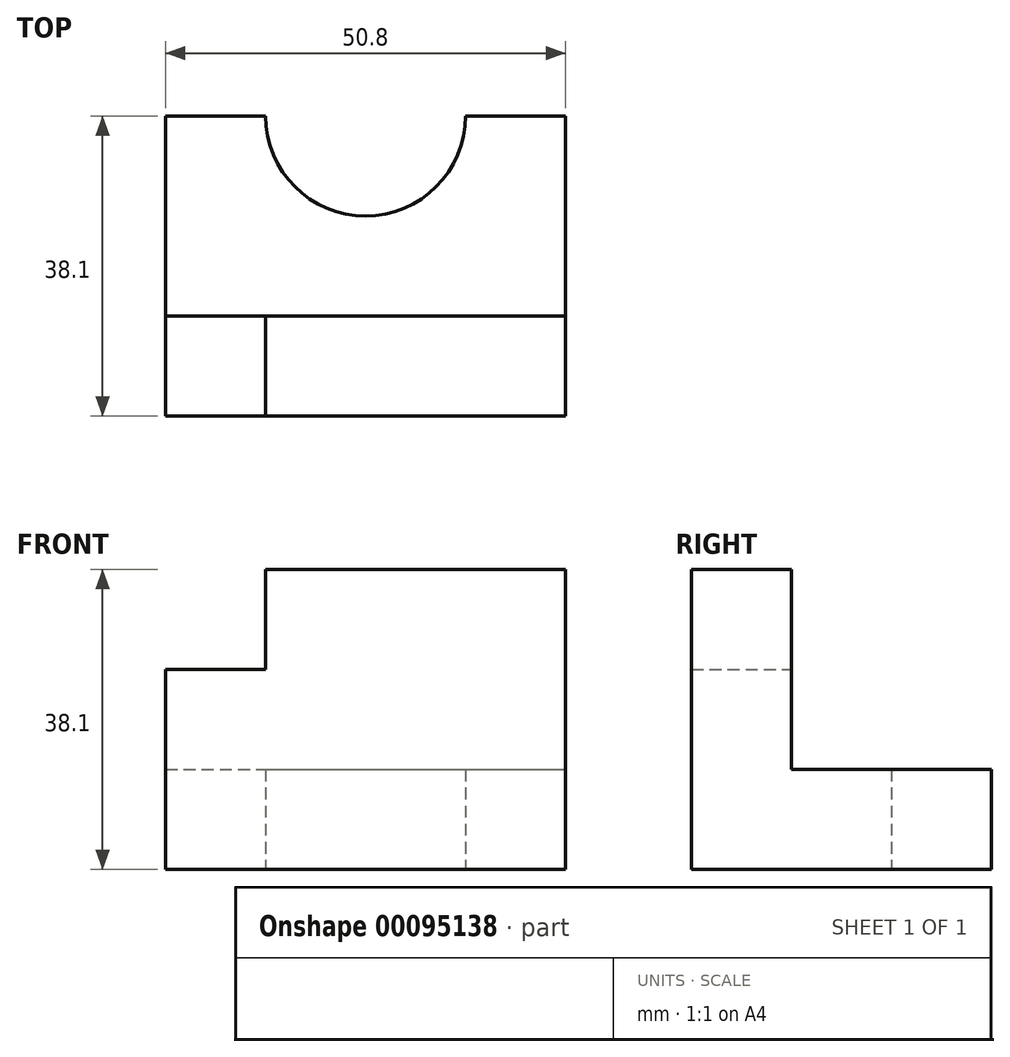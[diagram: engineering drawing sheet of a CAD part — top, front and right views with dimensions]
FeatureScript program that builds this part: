
annotation { "Feature Type Name" : "Feature", "Feature Type Description" : "" }
export const myFeature = defineFeature(function(context is Context, id is Id, definition is map)
    precondition{}
    {
        {
            var Q0;
            Q0=qCreatedBy(makeId("Top.planeOp"),FACE);
            var sketch = newSketch(context, id + "F0", { "sketchPlane" : qUnion([Q0])});
            skLineSegment(sketch, "E0.bottom", {"start": v(-25.4, 0) * mm, "end": v(25.4, 0) * mm});
            skLineSegment(sketch, "E0.top", {"start": v(-25.4, 38.1) * mm, "end": v(25.4, 38.1) * mm});
            skLineSegment(sketch, "E0.left", {"start": v(-25.4, 0) * mm, "end": v(-25.4, 38.1) * mm});
            skLineSegment(sketch, "E0.right", {"start": v(25.4, 0) * mm, "end": v(25.4, 38.1) * mm});
            skArc(sketch, "E1", {"start": v(-25.4, 38.1) * mm, "mid": v(0, 63.5) * mm, "end": v(25.4, 38.1) * mm});
            skCircle(sketch, "E2", {"center": v(0, 38.1) * mm, "radius": 12.7 * mm});
            skSolve(sketch);
        }
        {
            var Q0;
            Q0=makeQuery(id+"F0.imprint","IMPRINT",FACE,{"disambiguationData":[TD([[makeQuery(id+"F0.imprint","IMPRINT",EDGE,{"derivedFrom":sQuery(id+"F0.wireOp",EDGE,"E0.bottom")}),1.0]])]});
            var Q1;
            {var subQ0=sQuery(id+"F0.wireOp",EDGE,"E1");Q1=makeQuery(id+"F0.imprint","IMPRINT",FACE,{"disambiguationData":[TD([[makeQuery(id+"F0.imprint","IMPRINT",EDGE,{"derivedFrom":subQ0}),-1.0]])]});}
            extrude(context, id + "F1", {"entities" : qUnion([Q0, Q1]), "depth" : 12.7 * mm});
        }
        {
            var Q0;
            Q0=makeQuery(id+"F1.opExtrude","CAP_FACE",FACE,{"disambiguationData":[OSD([sQuery(id+"F0.wireOp",EDGE,"E0.bottom"),sQuery(id+"F0.wireOp",EDGE,"E0.left"),sQuery(id+"F0.wireOp",EDGE,"E0.right"),sQuery(id+"F0.wireOp",EDGE,"E1"),sQuery(id+"F0.wireOp",EDGE,"E2")])],"isStart":false});
            var sketch = newSketch(context, id + "F2", { "sketchPlane" : qUnion([Q0])});
            skLineSegment(sketch, "E3.bottom", {"start": v(-25.4, 0) * mm, "end": v(25.4, 0) * mm});
            skLineSegment(sketch, "E3.top", {"start": v(-25.4, 12.7) * mm, "end": v(25.4, 12.7) * mm});
            skLineSegment(sketch, "E3.left", {"start": v(-25.4, 0) * mm, "end": v(-25.4, 12.7) * mm});
            skLineSegment(sketch, "E3.right", {"start": v(25.4, 0) * mm, "end": v(25.4, 12.7) * mm});
            skLineSegment(sketch, "E4.bottom", {"start": v(-25.4, 12.7) * mm, "end": v(-12.7, 12.7) * mm});
            skLineSegment(sketch, "E4.top", {"start": v(-25.4, 0) * mm, "end": v(-12.7, 0) * mm});
            skLineSegment(sketch, "E4.left", {"start": v(-25.4, 12.7) * mm, "end": v(-25.4, 0) * mm});
            skLineSegment(sketch, "E4.right", {"start": v(-12.7, 12.7) * mm, "end": v(-12.7, 0) * mm});
            skSolve(sketch);
        }
        {
            var Q0;
            Q0=makeQuery(id+"F2.imprint","IMPRINT",FACE,{"disambiguationData":[TD([[makeQuery(id+"F2.imprint","IMPRINT",EDGE,{"derivedFrom":sQuery(id+"F2.wireOp",EDGE,"E3.bottom")}),1.0]])]});
            var Q1;
            Q1=makeQuery(id+"F2.imprint","IMPRINT",FACE,{"disambiguationData":[TD([[makeQuery(id+"F2.imprint","IMPRINT",EDGE,{"derivedFrom":sQuery(id+"F2.wireOp",EDGE,"E4.bottom")}),-1.0]])]});
            extrude(context, id + "F3", {"entities" : qUnion([Q0, Q1]), "operationType" : NewBodyOperationType.ADD, "depth" : 25.4 * mm});
        }
        {
            var Q0;
            Q0=makeQuery(id+"F3.opExtrude","CAP_FACE",FACE,{"disambiguationData":[OSD([sQuery(id+"F2.wireOp",EDGE,"E3.bottom"),sQuery(id+"F2.wireOp",EDGE,"E3.top"),sQuery(id+"F2.wireOp",EDGE,"E3.right"),sQuery(id+"F2.wireOp",EDGE,"E4.bottom"),sQuery(id+"F2.wireOp",EDGE,"E4.top"),sQuery(id+"F2.wireOp",EDGE,"E4.left")])],"isStart":false});
            var sketch = newSketch(context, id + "F4", { "sketchPlane" : qUnion([Q0])});
            skLineSegment(sketch, "E5.bottom", {"start": v(-25.4, 12.7) * mm, "end": v(-12.7, 12.7) * mm});
            skLineSegment(sketch, "E5.top", {"start": v(-25.4, 0) * mm, "end": v(-12.7, 0) * mm});
            skLineSegment(sketch, "E5.left", {"start": v(-25.4, 12.7) * mm, "end": v(-25.4, 0) * mm});
            skLineSegment(sketch, "E5.right", {"start": v(-12.7, 12.7) * mm, "end": v(-12.7, 0) * mm});
            skSolve(sketch);
        }
        {
            var Q0;
            Q0=makeQuery(id+"F4.imprint","IMPRINT",FACE,{"disambiguationData":[TD([[makeQuery(id+"F4.imprint","IMPRINT",EDGE,{"derivedFrom":sQuery(id+"F4.wireOp",EDGE,"E5.bottom")}),-1.0]])]});
            extrude(context, id + "F5", {"entities" : qUnion([Q0]), "operationType" : NewBodyOperationType.REMOVE, "oppositeDirection" : true, "depth" : 12.7 * mm});
        }
    });
